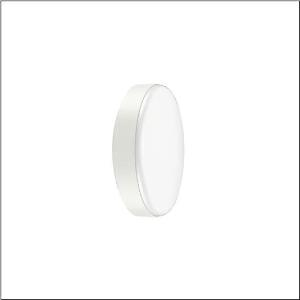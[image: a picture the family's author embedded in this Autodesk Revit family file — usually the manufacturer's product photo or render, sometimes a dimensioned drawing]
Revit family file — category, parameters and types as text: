
# Revit family: rondel_31_51wc10ma42as
name_source: partatom
category: Lighting Fixtures
units: mm (PartAtom-declared; Revit-internal decimal feet)

## family parameters
Cut with Voids When Loaded = No
Host = Face
Light Source = No
Part Type = Normal
Room Calculation Point = No
Round Connector Dimension = Use Diameter
Shared = No

## types (1)
- --- (1 x LED, 2550 lm, 20.5 W, 4000K)
    Apparent Load = 21 VA
    CIE Flux Codes = 44 75 94 94 100
    Color Rendering = 80
    Color Temperature = 4000K
    Default Elevation = 1800 mm
    Description = Rondel 31, wall and ceiling luminaire, primary optical cover: cover, of PC, opal, light emission: direct distribution, primary light characteristic: symmetric, installation type: surface-mounted, LED, rated luminous flux: 2.550lm, luminous efficacy: 124lm/W, light colour: 840, colour temperature: 4000K, with terminal, 3-pole, max. 2.5mm², mains connection: 220..240V, AC, 50/60Hz, rated input power: 20.5W, luminaire housing, of PC, traffic white (RAL 9016), diameter: 350mm, brightness and presence sensor, HF sensor, protection rating (complete): IP65, insulation class (complete): insulation class II (safety insulation), certification: CE, impact resistance: IK10, permissible operating ambient temperature: -20..+40°C, permissible storage temperature: -20..+60°C, packaging unit: 1 piece
    Height = 97 mm
    Lamp = 1 x LED
    Lamp Light Flux = 2550 lm
    Lamp Power = 20.5 W
    Lamp count = 1
    Length = 350 mm
    Luminous efficacy = 124 lm/W
    Manufacturer = Siteco
    ModVariant = No
    Model = 51WC10MA42AS
    Mounting Place = Ceiling
    Mounting Type = Surface mounted
    Number of Poles = 1
    OnlyDefault = Yes
    Power Factor = 1
    Product Name = Rondel 31
    Product group = wall and ceiling luminaire
    ProductGroupID = 301
    Protection Class = Protection class II
    Protection Degree = IP 65
    RLX_Detail_Level = 1
    RLX_Emergency_Light_Flux = 0 lm
    RLX_Emergency_Type = 0
    RLX_Emergency_Type_DB = No
    RlxData = <blob elided: 30413 chars, md5=fbca72fc>
    Socket = socket
    Standby Power = 0 W
    System Light Flux = 2550 lm
    System Power = 21 W
    Type Comments = factory setting: luminous flux: 100 % | (ON | ON)
    Type Image = l_1007027.jpg
    URL = http://relux.com
    VarID = @adj_083023
    Voltage = 0 V
    Weight = 0.00 kg
    Width = 0 mm  [stored 0 ft]

note: [stored X ft] marks values corroborated as IEEE doubles in the binary element streams (Revit-internal decimal feet)

## geometry (parser evidence)
native form markers: Blend x4, Sweep x12
no freeform markers — native parametric forms only
